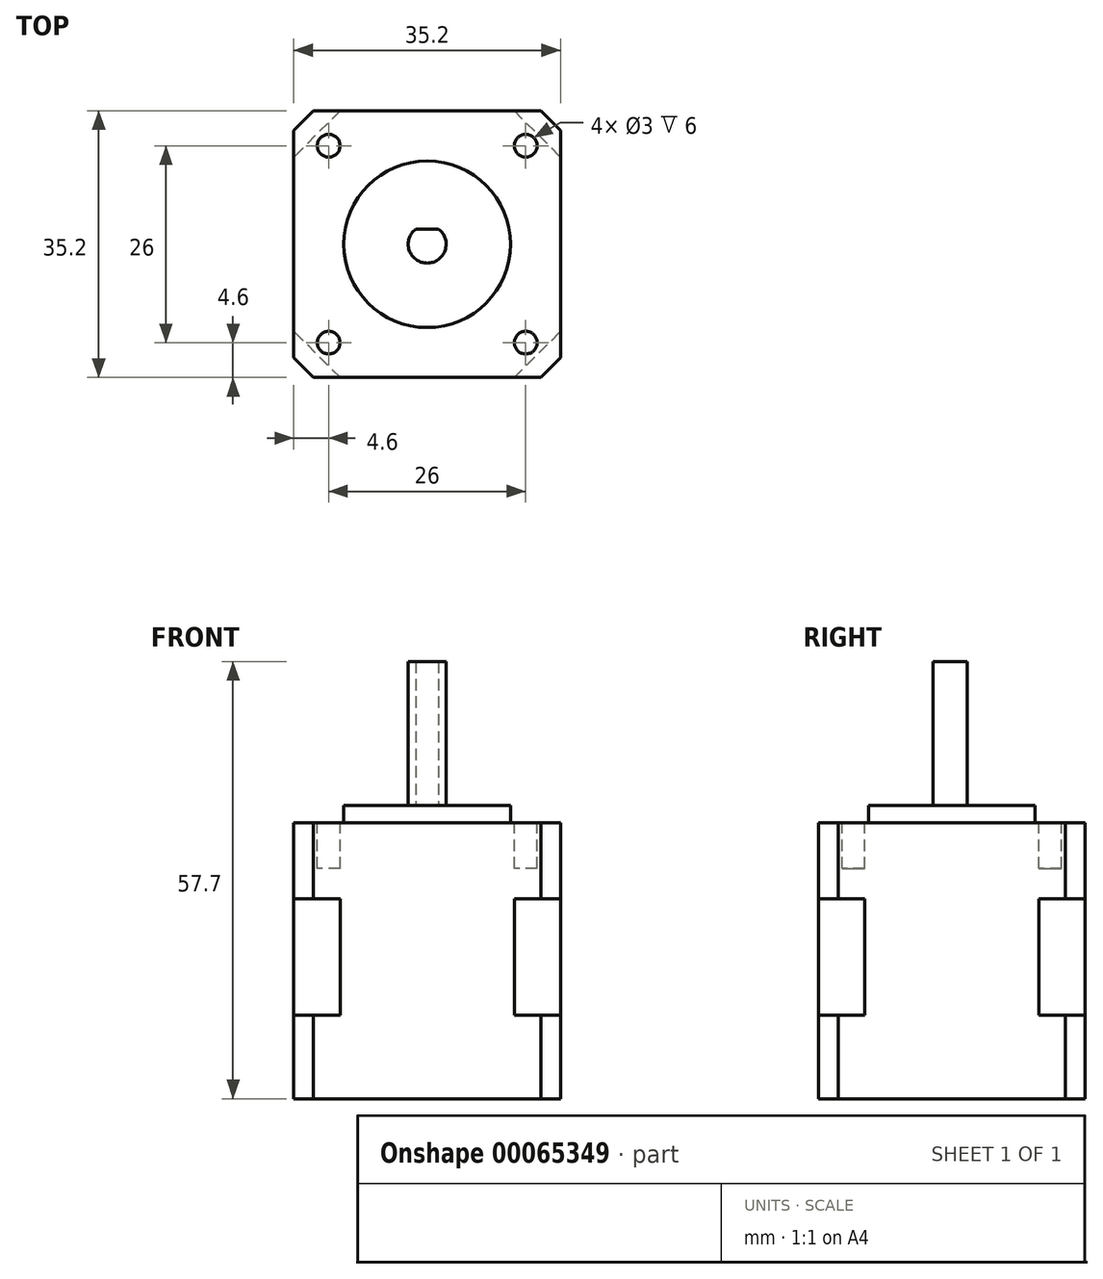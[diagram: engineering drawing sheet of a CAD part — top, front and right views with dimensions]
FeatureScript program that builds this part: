
annotation { "Feature Type Name" : "Feature", "Feature Type Description" : "" }
export const myFeature = defineFeature(function(context is Context, id is Id, definition is map)
    precondition{}
    {
        {
            var Q0;
            Q0=qCreatedBy(makeId("Top.planeOp"),FACE);
            var sketch = newSketch(context, id + "F0", { "sketchPlane" : qUnion([Q0])});
            skLineSegment(sketch, "E0.rect.bottom", {"start": v(-17.6, 17.6) * mm, "end": v(17.6, 17.6) * mm});
            skLineSegment(sketch, "E0.rect.top", {"start": v(-17.6, -17.6) * mm, "end": v(17.6, -17.6) * mm});
            skLineSegment(sketch, "E0.rect.left", {"start": v(-17.6, 17.6) * mm, "end": v(-17.6, -17.6) * mm});
            skLineSegment(sketch, "E0.rect.right", {"start": v(17.6, 17.6) * mm, "end": v(17.6, -17.6) * mm});
            skPoint(sketch, "E0.rect.middle", {"position": v(0, 0) * mm});
            skLineSegment(sketch, "E1", {"start": v(-17.6, 17.6) * mm, "end": v(17.6, -17.6) * mm, "construction": true});
            skSolve(sketch);
        }
        {
            var Q0;
            Q0=qSketchRegion(id+"F0",true);
            extrude(context, id + "F1", {"entities" : qUnion([Q0]), "endBound" : BoundingType.SYMMETRIC, "depth" : 15.4 * mm});
        }
        {
            var Q0;
            Q0=makeQuery(id+"F1.opExtrude","SWEPT_EDGE",EDGE,{"disambiguationData":[OSD([sQuery(id+"F0.wireOp",EDGE,"E0.rect.top"),sQuery(id+"F0.wireOp",EDGE,"E0.rect.left")])]});
            var Q1;
            Q1=makeQuery(id+"F1.opExtrude","SWEPT_EDGE",EDGE,{"disambiguationData":[OSD([sQuery(id+"F0.wireOp",EDGE,"E0.rect.top"),sQuery(id+"F0.wireOp",EDGE,"E0.rect.right")])]});
            var Q2;
            Q2=makeQuery(id+"F1.opExtrude","SWEPT_EDGE",EDGE,{"disambiguationData":[OSD([sQuery(id+"F0.wireOp",EDGE,"E0.rect.bottom"),sQuery(id+"F0.wireOp",EDGE,"E0.rect.right")])]});
            var Q3;
            Q3=makeQuery(id+"F1.opExtrude","SWEPT_EDGE",EDGE,{"disambiguationData":[OSD([sQuery(id+"F0.wireOp",EDGE,"E0.rect.bottom"),sQuery(id+"F0.wireOp",EDGE,"E0.rect.left")])]});
            chamfer(context, id + "F2", {"entities" : qUnion([Q0, Q1, Q2, Q3]), "width" : 6.1 * mm, "tangentPropagation" : true});
        }
        {
            var Q0;
            Q0=makeQuery(id+"F1.opExtrude","CAP_FACE",FACE,{"disambiguationData":[OSD([sQuery(id+"F0.wireOp",EDGE,"E0.rect.bottom"),sQuery(id+"F0.wireOp",EDGE,"E0.rect.top"),sQuery(id+"F0.wireOp",EDGE,"E0.rect.left"),sQuery(id+"F0.wireOp",EDGE,"E0.rect.right")])],"isStart":false});
            var sketch = newSketch(context, id + "F3", { "sketchPlane" : qUnion([Q0])});
            skLineSegment(sketch, "E2.0", {"start": v(-17.6, 17.6) * mm, "end": v(17.6, 17.6) * mm});
            skLineSegment(sketch, "E2.1", {"start": v(-17.6, -17.6) * mm, "end": v(17.6, -17.6) * mm});
            skLineSegment(sketch, "E2.2", {"start": v(-17.6, 17.6) * mm, "end": v(-17.6, -17.6) * mm});
            skLineSegment(sketch, "E2.3", {"start": v(17.6, 17.6) * mm, "end": v(17.6, -17.6) * mm});
            skPoint(sketch, "E2.4", {"position": v(0, 0) * mm});
            skSolve(sketch);
        }
        {
            var Q0;
            Q0=qSketchRegion(id+"F3",true);
            extrude(context, id + "F4", {"entities" : qUnion([Q0]), "operationType" : NewBodyOperationType.ADD, "depth" : 10 * mm});
        }
        {
            var Q0;
            Q0=makeQuery(id+"F4.opExtrude","SWEPT_EDGE",EDGE,{"disambiguationData":[OSD([sQuery(id+"F3.wireOp",EDGE,"E2.1"),sQuery(id+"F3.wireOp",EDGE,"E2.2")])]});
            var Q1;
            Q1=makeQuery(id+"F4.opExtrude","SWEPT_EDGE",EDGE,{"disambiguationData":[OSD([sQuery(id+"F3.wireOp",EDGE,"E2.1"),sQuery(id+"F3.wireOp",EDGE,"E2.3")])]});
            var Q2;
            Q2=makeQuery(id+"F4.opExtrude","SWEPT_EDGE",EDGE,{"disambiguationData":[OSD([sQuery(id+"F3.wireOp",EDGE,"E2.0"),sQuery(id+"F3.wireOp",EDGE,"E2.3")])]});
            var Q3;
            Q3=makeQuery(id+"F4.opExtrude","SWEPT_EDGE",EDGE,{"disambiguationData":[OSD([sQuery(id+"F3.wireOp",EDGE,"E2.0"),sQuery(id+"F3.wireOp",EDGE,"E2.2")])]});
            chamfer(context, id + "F5", {"entities" : qUnion([Q0, Q1, Q2, Q3]), "width" : 2.6 * mm, "tangentPropagation" : true});
        }
        {
            var Q0;
            Q0=makeQuery(id+"F1.opExtrude","CAP_FACE",FACE,{"disambiguationData":[OSD([sQuery(id+"F0.wireOp",EDGE,"E0.rect.bottom"),sQuery(id+"F0.wireOp",EDGE,"E0.rect.top"),sQuery(id+"F0.wireOp",EDGE,"E0.rect.left"),sQuery(id+"F0.wireOp",EDGE,"E0.rect.right")])],"isStart":true});
            var sketch = newSketch(context, id + "F6", { "sketchPlane" : qUnion([Q0])});
            skLineSegment(sketch, "E3.0.0", {"start": v(15, -17.6) * mm, "end": v(-15, -17.6) * mm});
            skLineSegment(sketch, "E3.0.1", {"start": v(-15, -17.6) * mm, "end": v(-17.6, -15) * mm});
            skLineSegment(sketch, "E3.0.2", {"start": v(-17.6, -15) * mm, "end": v(-17.6, 15) * mm});
            skLineSegment(sketch, "E3.0.3", {"start": v(-17.6, 15) * mm, "end": v(-15, 17.6) * mm});
            skLineSegment(sketch, "E3.0.4", {"start": v(-15, 17.6) * mm, "end": v(15, 17.6) * mm});
            skLineSegment(sketch, "E3.0.5", {"start": v(15, 17.6) * mm, "end": v(17.6, 15) * mm});
            skLineSegment(sketch, "E3.0.6", {"start": v(17.6, 15) * mm, "end": v(17.6, -15) * mm});
            skLineSegment(sketch, "E3.0.7", {"start": v(17.6, -15) * mm, "end": v(15, -17.6) * mm});
            skSolve(sketch);
        }
        {
            var Q0;
            Q0=qSketchRegion(id+"F6",true);
            extrude(context, id + "F7", {"entities" : qUnion([Q0]), "operationType" : NewBodyOperationType.ADD, "depth" : 11 * mm});
        }
        {
            var Q0;
            Q0=makeQuery(id+"F4.opExtrude","CAP_FACE",FACE,{"disambiguationData":[OSD([sQuery(id+"F3.wireOp",EDGE,"E2.0"),sQuery(id+"F3.wireOp",EDGE,"E2.1"),sQuery(id+"F3.wireOp",EDGE,"E2.2"),sQuery(id+"F3.wireOp",EDGE,"E2.3")])],"isStart":false});
            var sketch = newSketch(context, id + "F8", { "sketchPlane" : qUnion([Q0])});
            skCircle(sketch, "E4", {"center": v(0, 0) * mm, "radius": 11 * mm});
            skSolve(sketch);
        }
        {
            var Q0;
            Q0=qSketchRegion(id+"F8",true);
            extrude(context, id + "F9", {"entities" : qUnion([Q0]), "operationType" : NewBodyOperationType.ADD, "depth" : 2.3 * mm});
        }
        {
            var Q0;
            Q0=makeQuery(id+"F9.opExtrude","CAP_FACE",FACE,{"disambiguationData":[OSD([sQuery(id+"F8.wireOp",EDGE,"E4")])],"isStart":false});
            var sketch = newSketch(context, id + "F10", { "sketchPlane" : qUnion([Q0])});
            skCircle(sketch, "E5", {"center": v(0, 0) * mm, "radius": 2.5 * mm});
            skSolve(sketch);
        }
        {
            var Q0;
            Q0=makeQuery(id+"F10.imprint","IMPRINT",FACE,{"disambiguationData":[TD([[makeQuery(id+"F10.imprint","IMPRINT",EDGE,{"derivedFrom":sQuery(id+"F10.wireOp",EDGE,"E5")}),1.0]])]});
            extrude(context, id + "F11", {"entities" : qUnion([Q0]), "operationType" : NewBodyOperationType.ADD, "depth" : 19 * mm});
        }
        {
            var Q0;
            Q0=makeQuery(id+"F11.opExtrude","CAP_FACE",FACE,{"disambiguationData":[OSD([sQuery(id+"F10.wireOp",EDGE,"E5")])],"isStart":false});
            var sketch = newSketch(context, id + "F12", { "sketchPlane" : qUnion([Q0])});
            skLineSegment(sketch, "E6.bottom", {"start": v(-2.63, 2.93) * mm, "end": v(2.62, 2.93) * mm});
            skLineSegment(sketch, "E6.top", {"start": v(-2.63, 2) * mm, "end": v(2.62, 2) * mm});
            skLineSegment(sketch, "E6.left", {"start": v(-2.63, 2.93) * mm, "end": v(-2.63, 2) * mm});
            skLineSegment(sketch, "E6.right", {"start": v(2.62, 2.93) * mm, "end": v(2.62, 2) * mm});
            skSolve(sketch);
        }
        {
            var Q0;
            Q0=qSketchRegion(id+"F12",true);
            extrude(context, id + "F13", {"entities" : qUnion([Q0]), "operationType" : NewBodyOperationType.REMOVE, "oppositeDirection" : true, "depth" : 19 * mm});
        }
        {
            var Q0;
            Q0=makeQuery(id+"F4.opExtrude","CAP_FACE",FACE,{"disambiguationData":[OSD([sQuery(id+"F3.wireOp",EDGE,"E2.0"),sQuery(id+"F3.wireOp",EDGE,"E2.1"),sQuery(id+"F3.wireOp",EDGE,"E2.2"),sQuery(id+"F3.wireOp",EDGE,"E2.3")])],"isStart":false});
            var sketch = newSketch(context, id + "F14", { "sketchPlane" : qUnion([Q0])});
            skCircle(sketch, "E7", {"center": v(-13, 13) * mm, "radius": 1.5 * mm});
            skCircle(sketch, "E8.MirrorC", {"center": v(13, 13) * mm, "radius": 1.5 * mm});
            skCircle(sketch, "E9.MirrorC", {"center": v(-13, -13) * mm, "radius": 1.5 * mm});
            skCircle(sketch, "E10.MirrorC", {"center": v(13, -13) * mm, "radius": 1.5 * mm});
            skLineSegment(sketch, "E11", {"start": v(-13, 13) * mm, "end": v(13, -13) * mm, "construction": true});
            skLineSegment(sketch, "E12.rect.bottom", {"start": v(-13, 13) * mm, "end": v(13, 13) * mm, "construction": true});
            skLineSegment(sketch, "E12.rect.top", {"start": v(-13, -13) * mm, "end": v(13, -13) * mm, "construction": true});
            skLineSegment(sketch, "E12.rect.left", {"start": v(-13, 13) * mm, "end": v(-13, -13) * mm, "construction": true});
            skLineSegment(sketch, "E12.rect.right", {"start": v(13, 13) * mm, "end": v(13, -13) * mm, "construction": true});
            skPoint(sketch, "E12.rect.middle", {"position": v(0, 0) * mm});
            skSolve(sketch);
        }
        {
            var Q0;
            Q0=qSketchRegion(id+"F14",true);
            extrude(context, id + "F15", {"entities" : qUnion([Q0]), "operationType" : NewBodyOperationType.REMOVE, "oppositeDirection" : true, "depth" : 6 * mm});
        }
    });
